# Revit family: Haworth_Immerse_StackTable_RectangleTwoPieceTop
name_source: partatom
category: Furniture Systems
revit_build: Autodesk Revit 2018 (Build: 20170223_1515(x64)
units: mm (PartAtom-declared; Revit-internal decimal feet)

## family parameters
Always vertical = Yes
Cut with Voids When Loaded = No
OmniClass Number = 23.40.70.14.64.21
OmniClass Title = Systems Furniture
Part Type = Normal
Room Calculation Point = No
Round Connector Dimension = Use Diameter
Shared = No
Work Plane-Based = No

## types (1)
- 60d 144w 39h - Oblong Planter
    Actual Depth = 60"
    Actual Height = 39"
    Actual Width = 144"
    Assembly Code = E2020200
    Description = Haworth Immerse Stack Table Rectangle Two Piece Top - 60d 144w 39h - Oblong Planter
    Lower Top Cutout Depth = 12 1/2"
    Lower Top Cutout Width = 78"
    Lower Top Thickness = 1/8"
    Lower Top Width = 142"
    Manufacturer = Haworth
    Model = THRA-60E4
    Oblong Planter = Yes
    Oblong Planter Void Height = 6"
    Revision Number = 1
    Size = Verify Final Dim. w/ Haworth
    Standard Height = 39 in.
    Standard Sizes = 60d 144w
    URL = https://www.haworth.com
    URL - Product = http://www.haworth.com
    Understructure Overall Width = 81"
    Understucture Thickness = 3 1/2"
    Upper Top Thickness = 1 3/16"
    Warranty = http://www.haworth.com

## geometry (parser evidence)
native form markers: Sweep x5
no freeform markers — native parametric forms only
